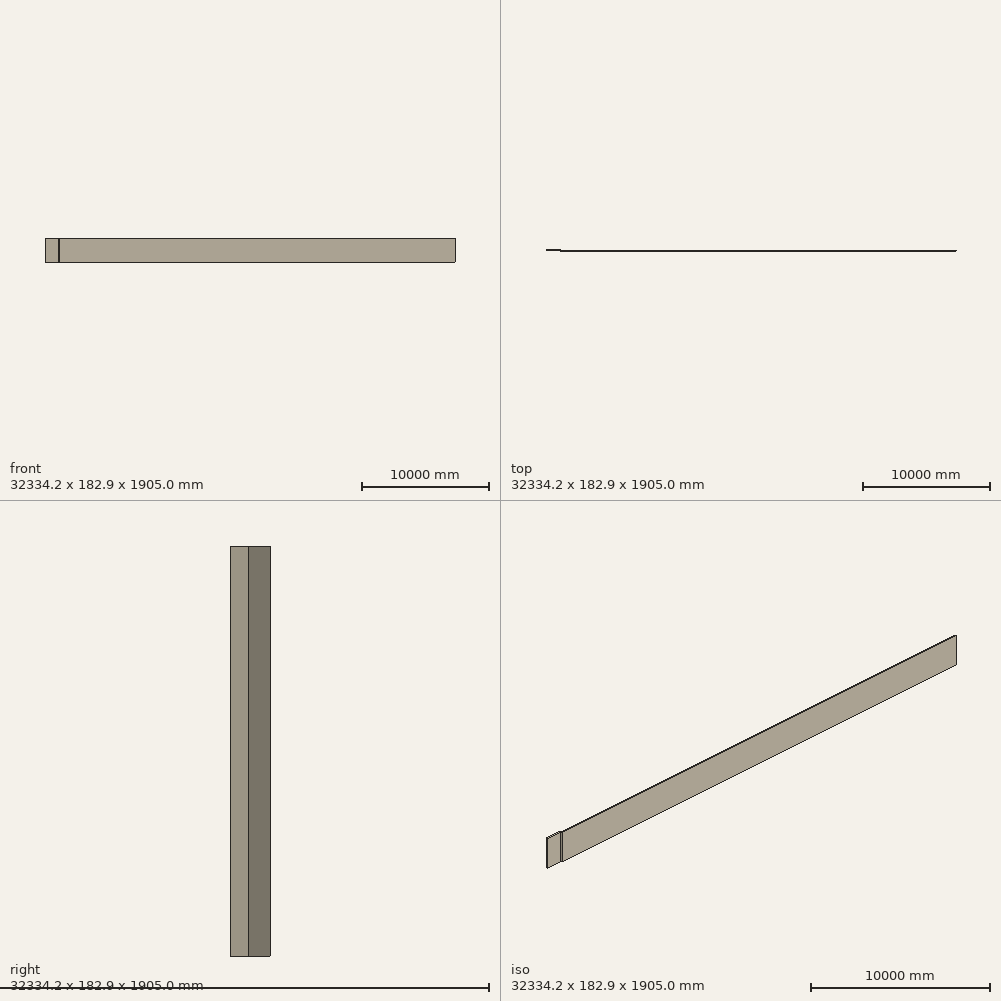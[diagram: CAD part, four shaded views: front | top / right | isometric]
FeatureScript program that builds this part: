
annotation { "Feature Type Name" : "Feature", "Feature Type Description" : "" }
export const myFeature = defineFeature(function(context is Context, id is Id, definition is map)
    precondition{}
    {
        {
            var Q0;
            Q0=qCreatedBy(makeId("Top.planeOp"),FACE);
            var sketch = newSketch(context, id + "F0", { "sketchPlane" : qUnion([Q0])});
            skLineSegment(sketch, "E0.0", {"start": v(-15312.16, 23.22) * mm, "end": v(15904.44, 23.22) * mm});
            skLineSegment(sketch, "E1.0", {"start": v(-16429.76, 104.5) * mm, "end": v(-15393.44, 104.5) * mm});
            skLineSegment(sketch, "E2", {"start": v(15904.44, 104.5) * mm, "end": v(15904.44, 23.22) * mm});
            skLineSegment(sketch, "E3", {"start": v(-16429.76, 104.5) * mm, "end": v(-16429.76, 206.1) * mm});
            skLineSegment(sketch, "E4", {"start": v(-16429.76, 206.1) * mm, "end": v(-15380.1, 206.1) * mm});
            skLineSegment(sketch, "E5", {"start": v(-15312.16, 23.22) * mm, "end": v(-15393.44, 104.5) * mm});
            skLineSegment(sketch, "E6.0", {"start": v(-15278.5, 104.5) * mm, "end": v(-15380.1, 206.1) * mm});
            skLineSegment(sketch, "E7.trimOffspring", {"start": v(-15278.5, 104.5) * mm, "end": v(15904.44, 104.5) * mm});
            skSolve(sketch);
        }
        {
            var Q0;
            Q0 = qSketchRegion(id + "F0", true);
            extrude(context, id + "F1", {"entities" : qUnion([Q0]), "depth" : 1905 * mm, "offsetDistance" : 25.4 * mm});
        }
    });
